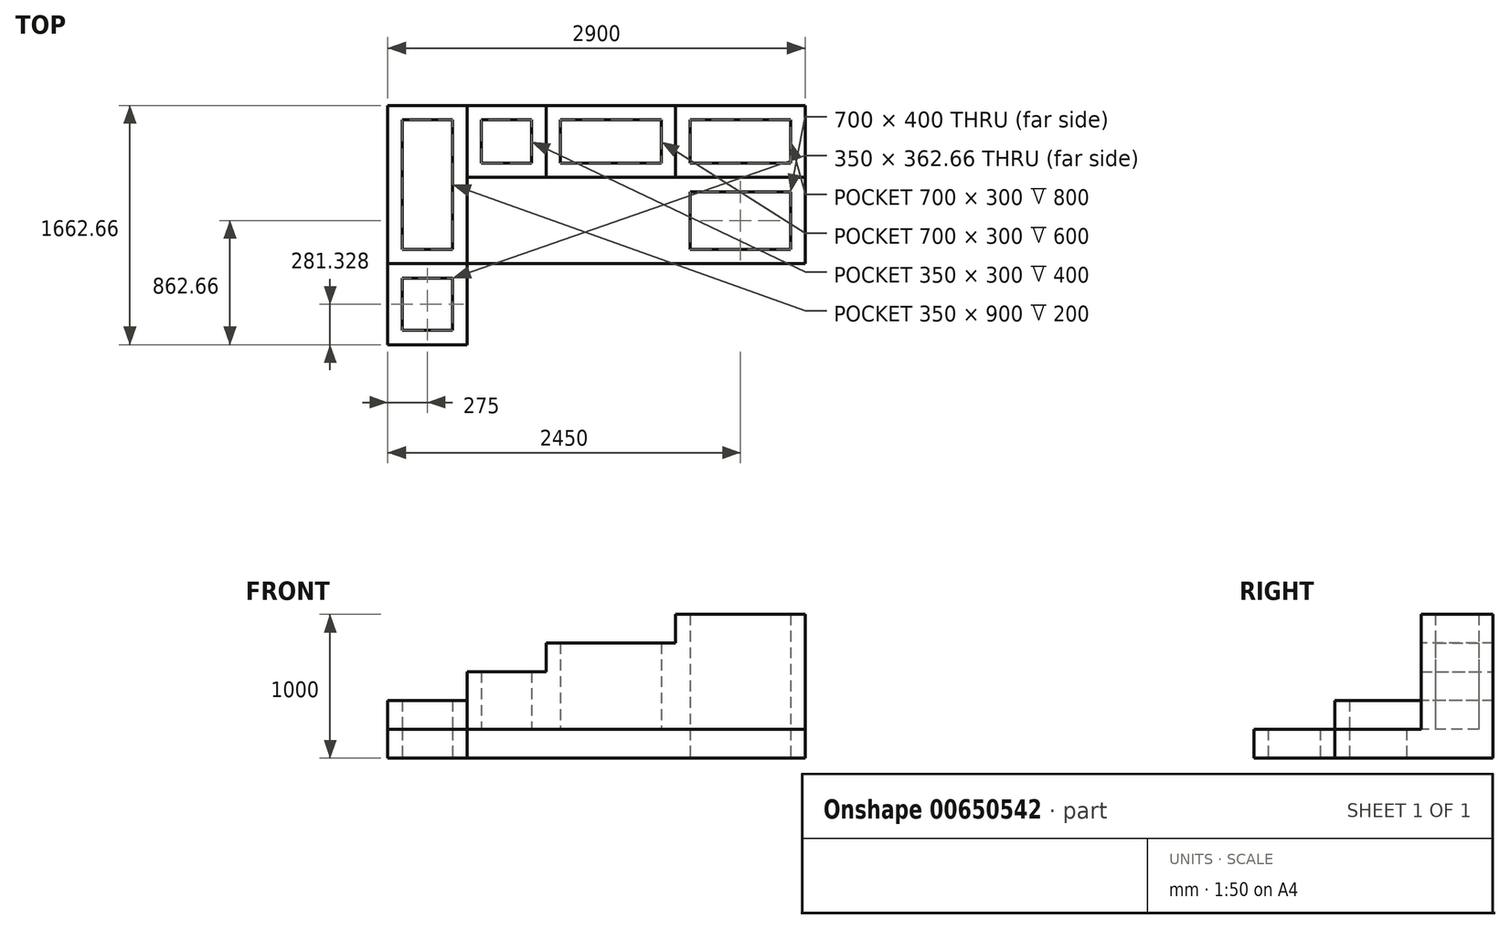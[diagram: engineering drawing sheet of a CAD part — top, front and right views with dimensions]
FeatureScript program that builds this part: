
annotation { "Feature Type Name" : "Feature", "Feature Type Description" : "" }
export const myFeature = defineFeature(function(context is Context, id is Id, definition is map)
    precondition{}
    {
        {
            var Q0;
            Q0=qCreatedBy(makeId("Top.planeOp"),FACE);
            var sketch = newSketch(context, id + "F0", { "sketchPlane" : qUnion([Q0])});
            skLineSegment(sketch, "E0.bottom", {"start": v(0, 0) * mm, "end": v(-2350, 0) * mm});
            skLineSegment(sketch, "E0.top", {"start": v(0, 1100) * mm, "end": v(-2900, 1100) * mm});
            skLineSegment(sketch, "E0.left", {"start": v(0, 0) * mm, "end": v(0, 1100) * mm});
            skLineSegment(sketch, "E0.right", {"start": v(-2900, 0) * mm, "end": v(-2900, 1100) * mm});
            skLineSegment(sketch, "E1.bottom", {"start": v(-100, 100) * mm, "end": v(-800, 100) * mm});
            skLineSegment(sketch, "E1.top", {"start": v(-100, 500) * mm, "end": v(-800, 500) * mm});
            skLineSegment(sketch, "E1.left", {"start": v(-100, 100) * mm, "end": v(-100, 500) * mm});
            skLineSegment(sketch, "E1.right", {"start": v(-800, 100) * mm, "end": v(-800, 500) * mm});
            skLineSegment(sketch, "E2.top", {"start": v(-2900, -562.66) * mm, "end": v(-2350, -562.66) * mm});
            skLineSegment(sketch, "E2.left", {"start": v(-2900, 0) * mm, "end": v(-2900, -562.66) * mm});
            skLineSegment(sketch, "E2.right", {"start": v(-2350, 0) * mm, "end": v(-2350, -562.66) * mm});
            skLineSegment(sketch, "E3.bottom", {"start": v(-2800, -100) * mm, "end": v(-2450, -100) * mm});
            skLineSegment(sketch, "E3.top", {"start": v(-2800, -462.66) * mm, "end": v(-2450, -462.66) * mm});
            skLineSegment(sketch, "E3.left", {"start": v(-2800, -100) * mm, "end": v(-2800, -462.66) * mm});
            skLineSegment(sketch, "E3.right", {"start": v(-2450, -100) * mm, "end": v(-2450, -462.66) * mm});
            skSolve(sketch);
        }
        {
            var Q0;
            Q0=makeQuery(id+"F0.imprint","IMPRINT",FACE,{"disambiguationData":[TD([[makeQuery(id+"F0.imprint","IMPRINT",EDGE,{"derivedFrom":sQuery(id+"F0.wireOp",EDGE,"E0.bottom")}),-1.0]])]});
            extrude(context, id + "F1", {"entities" : qUnion([Q0]), "depth" : 200 * mm, "offsetDistance" : 25 * mm});
        }
        {
            var Q0;
            Q0=makeQuery(id+"F1.opExtrude","CAP_FACE",FACE,{"disambiguationData":[OSD([sQuery(id+"F0.wireOp",EDGE,"E0.bottom"),sQuery(id+"F0.wireOp",EDGE,"E0.top"),sQuery(id+"F0.wireOp",EDGE,"E0.left"),sQuery(id+"F0.wireOp",EDGE,"E0.right"),sQuery(id+"F0.wireOp",EDGE,"E1.bottom"),sQuery(id+"F0.wireOp",EDGE,"E1.top"),sQuery(id+"F0.wireOp",EDGE,"E1.left"),sQuery(id+"F0.wireOp",EDGE,"E1.right")])],"isStart":false});
            var sketch = newSketch(context, id + "F2", { "sketchPlane" : qUnion([Q0])});
            skLineSegment(sketch, "E4.bottom", {"start": v(0, 1100) * mm, "end": v(-900, 1100) * mm});
            skLineSegment(sketch, "E4.top", {"start": v(0, 600) * mm, "end": v(-900, 600) * mm});
            skLineSegment(sketch, "E4.left", {"start": v(0, 1100) * mm, "end": v(0, 600) * mm});
            skLineSegment(sketch, "E4.right", {"start": v(-900, 1100) * mm, "end": v(-900, 600) * mm});
            skLineSegment(sketch, "E5.bottom", {"start": v(-800, 1000) * mm, "end": v(-100, 1000) * mm});
            skLineSegment(sketch, "E5.top", {"start": v(-800, 700) * mm, "end": v(-100, 700) * mm});
            skLineSegment(sketch, "E5.left", {"start": v(-800, 1000) * mm, "end": v(-800, 700) * mm});
            skLineSegment(sketch, "E5.right", {"start": v(-100, 1000) * mm, "end": v(-100, 700) * mm});
            skSolve(sketch);
        }
        {
            var Q0;
            Q0 = qSketchRegion(id + "F2", true);
            extrude(context, id + "F3", {"entities" : qUnion([Q0]), "operationType" : NewBodyOperationType.ADD, "depth" : 800 * mm, "offsetDistance" : 25 * mm});
        }
        {
            var Q0;
            {var subQ0=sQuery(id+"F0.wireOp",EDGE,"E0.left");var subQ1=sQuery(id+"F0.wireOp",EDGE,"E1.right");var subQ2=sQuery(id+"F0.wireOp",EDGE,"E1.left");var subQ3=sQuery(id+"F0.wireOp",EDGE,"E1.top");var subQ4=sQuery(id+"F0.wireOp",EDGE,"E1.bottom");var subQ5=sQuery(id+"F0.wireOp",EDGE,"E0.bottom");var subQ6=sQuery(id+"F0.wireOp",EDGE,"E0.right");var subQ7=sQuery(id+"F0.wireOp",EDGE,"E0.top");Q0=makeQuery(id+"F3.boolean.opBoolean","SPLIT",FACE,{"disambiguationData":[TD([makeQuery(id+"F1.opExtrude","SWEPT_FACE",FACE,{"disambiguationData":[OSD([subQ5])]})])],"derivedFrom":makeQuery(id+"F1.opExtrude","CAP_FACE",FACE,{"disambiguationData":[OSD([subQ5,subQ7,subQ0,subQ6,subQ4,subQ3,subQ2,subQ1])],"isStart":false})});}
            var sketch = newSketch(context, id + "F4", { "sketchPlane" : qUnion([Q0])});
            skLineSegment(sketch, "E6.bottom", {"start": v(-900, 600) * mm, "end": v(-1800, 600) * mm});
            skLineSegment(sketch, "E6.top", {"start": v(-900, 1100) * mm, "end": v(-1800, 1100) * mm});
            skLineSegment(sketch, "E6.left", {"start": v(-900, 600) * mm, "end": v(-900, 1100) * mm});
            skLineSegment(sketch, "E6.right", {"start": v(-1800, 600) * mm, "end": v(-1800, 1100) * mm});
            skLineSegment(sketch, "E7.bottom", {"start": v(-1000, 700) * mm, "end": v(-1700, 700) * mm});
            skLineSegment(sketch, "E7.top", {"start": v(-1000, 1000) * mm, "end": v(-1700, 1000) * mm});
            skLineSegment(sketch, "E7.left", {"start": v(-1000, 700) * mm, "end": v(-1000, 1000) * mm});
            skLineSegment(sketch, "E7.right", {"start": v(-1700, 700) * mm, "end": v(-1700, 1000) * mm});
            skSolve(sketch);
        }
        {
            var Q0;
            Q0 = qSketchRegion(id + "F4", true);
            extrude(context, id + "F5", {"entities" : qUnion([Q0]), "operationType" : NewBodyOperationType.ADD, "depth" : 600 * mm, "offsetDistance" : 25 * mm});
        }
        {
            var Q0;
            {var subQ1=sQuery(id+"F0.wireOp",EDGE,"E0.left");var subQ3=sQuery(id+"F0.wireOp",EDGE,"E1.right");var subQ5=sQuery(id+"F0.wireOp",EDGE,"E1.left");var subQ8=sQuery(id+"F0.wireOp",EDGE,"E1.top");var subQ11=sQuery(id+"F0.wireOp",EDGE,"E1.bottom");var subQ13=sQuery(id+"F0.wireOp",EDGE,"E0.bottom");var subQ14=makeQuery(id+"F1.opExtrude","SWEPT_FACE",FACE,{"disambiguationData":[OSD([subQ13])]});var subQ15=sQuery(id+"F0.wireOp",EDGE,"E0.right");var subQ17=sQuery(id+"F0.wireOp",EDGE,"E0.top");Q0=makeQuery(id+"F5.boolean.opBoolean","SPLIT",FACE,{"disambiguationData":[TD([subQ14])],"derivedFrom":makeQuery(id+"F3.boolean.opBoolean","SPLIT",FACE,{"disambiguationData":[TD([subQ14])],"derivedFrom":makeQuery(id+"F1.opExtrude","CAP_FACE",FACE,{"disambiguationData":[OSD([subQ13,subQ17,subQ1,subQ15,subQ11,subQ8,subQ5,subQ3])],"isStart":false})})});}
            var sketch = newSketch(context, id + "F6", { "sketchPlane" : qUnion([Q0])});
            skLineSegment(sketch, "E8.bottom", {"start": v(-1800, 600) * mm, "end": v(-2350, 600) * mm});
            skLineSegment(sketch, "E8.top", {"start": v(-1800, 1100) * mm, "end": v(-2350, 1100) * mm});
            skLineSegment(sketch, "E8.left", {"start": v(-1800, 600) * mm, "end": v(-1800, 1100) * mm});
            skLineSegment(sketch, "E8.right", {"start": v(-2350, 600) * mm, "end": v(-2350, 1100) * mm});
            skLineSegment(sketch, "E9.bottom", {"start": v(-1900, 700) * mm, "end": v(-2250, 700) * mm});
            skLineSegment(sketch, "E9.top", {"start": v(-1900, 1000) * mm, "end": v(-2250, 1000) * mm});
            skLineSegment(sketch, "E9.left", {"start": v(-1900, 700) * mm, "end": v(-1900, 1000) * mm});
            skLineSegment(sketch, "E9.right", {"start": v(-2250, 700) * mm, "end": v(-2250, 1000) * mm});
            skSolve(sketch);
        }
        {
            var Q0;
            Q0 = qSketchRegion(id + "F6", true);
            extrude(context, id + "F7", {"entities" : qUnion([Q0]), "operationType" : NewBodyOperationType.ADD, "depth" : 400 * mm, "offsetDistance" : 25 * mm});
        }
        {
            var Q0;
            {var subQ1=sQuery(id+"F0.wireOp",EDGE,"E0.left");var subQ3=sQuery(id+"F0.wireOp",EDGE,"E1.right");var subQ5=sQuery(id+"F0.wireOp",EDGE,"E1.left");var subQ8=sQuery(id+"F0.wireOp",EDGE,"E1.top");var subQ11=sQuery(id+"F0.wireOp",EDGE,"E1.bottom");var subQ13=sQuery(id+"F0.wireOp",EDGE,"E0.bottom");var subQ14=makeQuery(id+"F1.opExtrude","SWEPT_FACE",FACE,{"disambiguationData":[OSD([subQ13])]});var subQ15=sQuery(id+"F0.wireOp",EDGE,"E0.right");var subQ17=sQuery(id+"F0.wireOp",EDGE,"E0.top");Q0=makeQuery(id+"F7.boolean.opBoolean","SPLIT",FACE,{"disambiguationData":[TD([subQ14])],"derivedFrom":makeQuery(id+"F5.boolean.opBoolean","SPLIT",FACE,{"disambiguationData":[TD([subQ14])],"derivedFrom":makeQuery(id+"F3.boolean.opBoolean","SPLIT",FACE,{"disambiguationData":[TD([subQ14])],"derivedFrom":makeQuery(id+"F1.opExtrude","CAP_FACE",FACE,{"disambiguationData":[OSD([subQ13,subQ17,subQ1,subQ15,subQ11,subQ8,subQ5,subQ3])],"isStart":false})})})});}
            var sketch = newSketch(context, id + "F8", { "sketchPlane" : qUnion([Q0])});
            skLineSegment(sketch, "E10.bottom", {"start": v(-2900, 1100) * mm, "end": v(-2350, 1100) * mm});
            skLineSegment(sketch, "E10.top", {"start": v(-2900, 0) * mm, "end": v(-2350, 0) * mm});
            skLineSegment(sketch, "E10.left", {"start": v(-2900, 1100) * mm, "end": v(-2900, 0) * mm});
            skLineSegment(sketch, "E10.right", {"start": v(-2350, 1100) * mm, "end": v(-2350, 0) * mm});
            skLineSegment(sketch, "E11.bottom", {"start": v(-2800, 1000) * mm, "end": v(-2450, 1000) * mm});
            skLineSegment(sketch, "E11.top", {"start": v(-2800, 100) * mm, "end": v(-2450, 100) * mm});
            skLineSegment(sketch, "E11.left", {"start": v(-2800, 1000) * mm, "end": v(-2800, 100) * mm});
            skLineSegment(sketch, "E11.right", {"start": v(-2450, 1000) * mm, "end": v(-2450, 100) * mm});
            skSolve(sketch);
        }
        {
            var Q0;
            Q0 = qSketchRegion(id + "F8", true);
            extrude(context, id + "F9", {"entities" : qUnion([Q0]), "operationType" : NewBodyOperationType.ADD, "depth" : 200 * mm, "offsetDistance" : 25 * mm});
        }
    });
